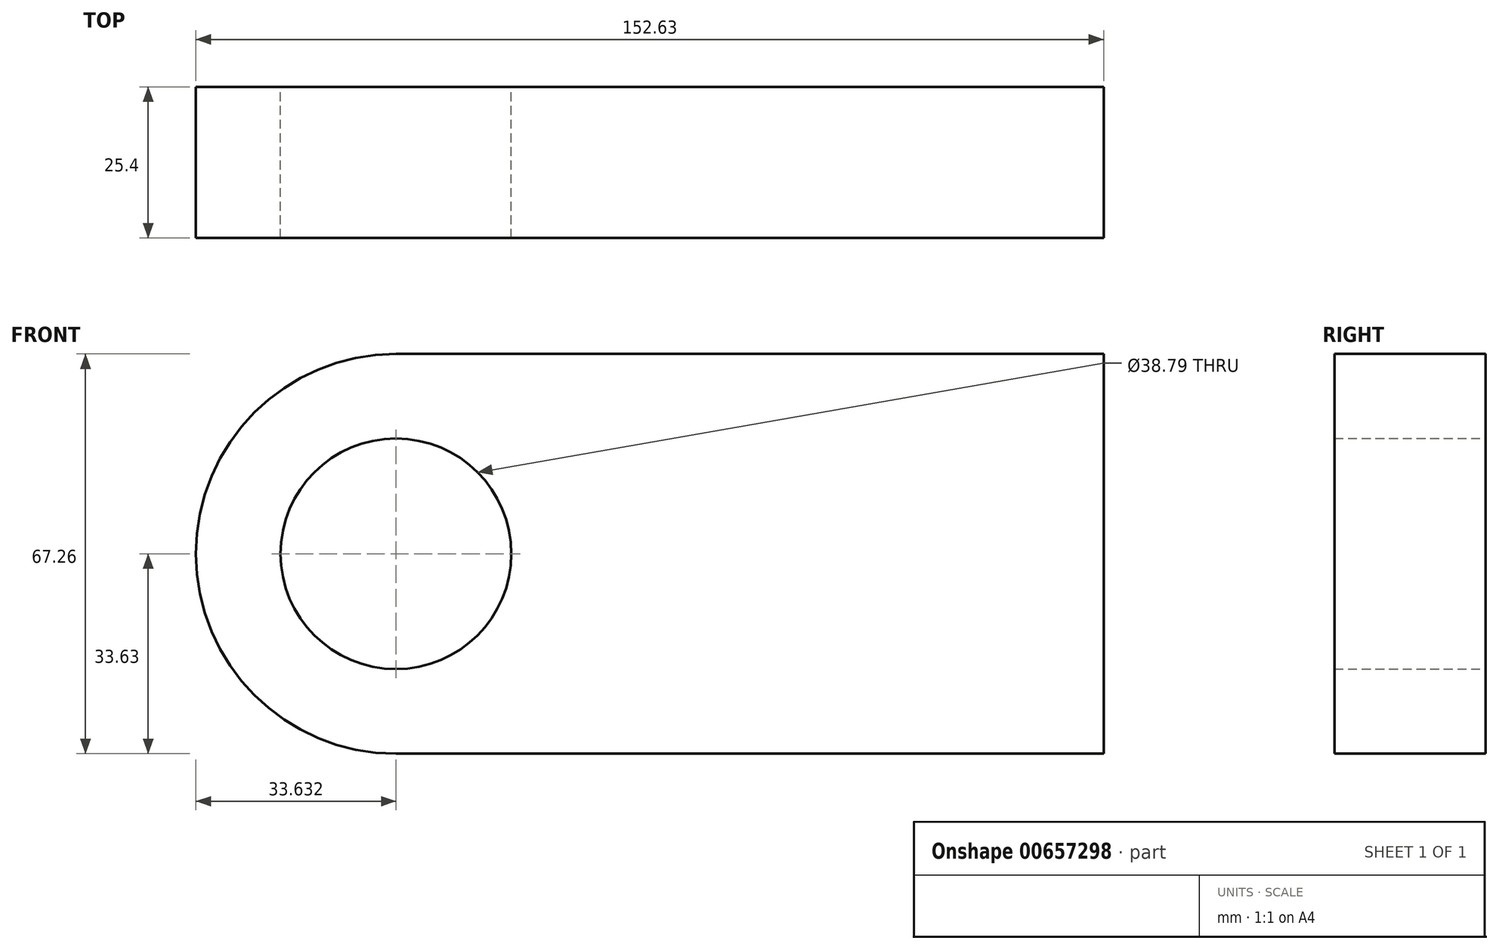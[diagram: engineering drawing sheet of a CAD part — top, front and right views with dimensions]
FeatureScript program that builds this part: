
annotation { "Feature Type Name" : "Feature", "Feature Type Description" : "" }
export const myFeature = defineFeature(function(context is Context, id is Id, definition is map)
    precondition{}
    {
        {
            var Q0;
            Q0=qCreatedBy(makeId("Front.planeOp"),FACE);
            var sketch = newSketch(context, id + "F0", { "sketchPlane" : qUnion([Q0])});
            skLineSegment(sketch, "E0.bottom", {"start": v(59.5, -33.63) * mm, "end": v(-59.5, -33.63) * mm});
            skLineSegment(sketch, "E0.top", {"start": v(59.5, 33.63) * mm, "end": v(-59.5, 33.63) * mm});
            skLineSegment(sketch, "E0.left", {"start": v(59.5, -33.63) * mm, "end": v(59.5, 33.63) * mm});
            skLineSegment(sketch, "E0.right", {"start": v(-59.5, -33.63) * mm, "end": v(-59.5, 33.63) * mm});
            skPoint(sketch, "E0.middle", {"position": v(0, 0) * mm});
            skCircle(sketch, "E1", {"center": v(-59.5, 0) * mm, "radius": 33.63 * mm});
            skCircle(sketch, "E2", {"center": v(-59.5, 0) * mm, "radius": 19.4 * mm});
            skSolve(sketch);
        }
        {
            var Q0;
            {var subQ0=sQuery(id+"F0.wireOp",EDGE,"E0.bottom");Q0=makeQuery(id+"F0.imprint","IMPRINT",FACE,{"disambiguationData":[TD([[makeQuery(id+"F0.imprint","IMPRINT",EDGE,{"derivedFrom":subQ0}),-1.0]])]});}
            var Q1;
            {var subQ1=sQuery(id+"F0.wireOp",EDGE,"E0.right");var subQ3=sQuery(id+"F0.wireOp",EDGE,"E2");var subQ4=makeQuery(id+"F0.imprint","INTERSECT",VERTEX,{"disambiguationData":[OD(0.0)],"derivedFrom":[subQ1,subQ3]});Q1=makeQuery(id+"F0.imprint","IMPRINT",FACE,{"disambiguationData":[TD([[makeQuery(id+"F0.imprint","IMPRINT",EDGE,{"disambiguationData":[TD([[subQ4,1.0]])],"derivedFrom":subQ3}),-1.0]])]});}
            var Q2;
            {var subQ1=sQuery(id+"F0.wireOp",EDGE,"E0.right");var subQ3=sQuery(id+"F0.wireOp",EDGE,"E2");var subQ4=makeQuery(id+"F0.imprint","INTERSECT",VERTEX,{"disambiguationData":[OD(0.0)],"derivedFrom":[subQ1,subQ3]});Q2=makeQuery(id+"F0.imprint","IMPRINT",FACE,{"disambiguationData":[TD([[makeQuery(id+"F0.imprint","IMPRINT",EDGE,{"disambiguationData":[TD([[subQ4,-1.0]])],"derivedFrom":subQ3}),-1.0]])]});}
            extrude(context, id + "F1", {"entities" : qUnion([Q0, Q1, Q2]), "depth" : 25.4 * mm, "offsetDistance" : 25.4 * mm});
        }
    });
